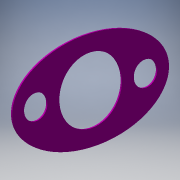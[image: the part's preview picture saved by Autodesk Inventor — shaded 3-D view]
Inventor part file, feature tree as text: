
AUTODESK INVENTOR PART (.ipt)
format: ipt  version: 2018 (Build 220112000, 112)  size: 108,544 bytes
history: native  units: mm
features: extrude x1, sketch x1
ambient origin geometry x8: Origin, YZ Plane, XZ Plane, XY Plane, X Axis, Y Axis, Z Axis, Center Point
bodies: Solid1 (feature_tree)
feature tree (2):
  extrude  "Extrusion1"  Depth=0.2mm
  sketch  "Sketch1"  dims[d0=3.0mm d1=8.0mm d3=7.0mm d4=7.0mm d5=20.0mm d6=12.0mm d7=0.2mm d8=0.0mm]
